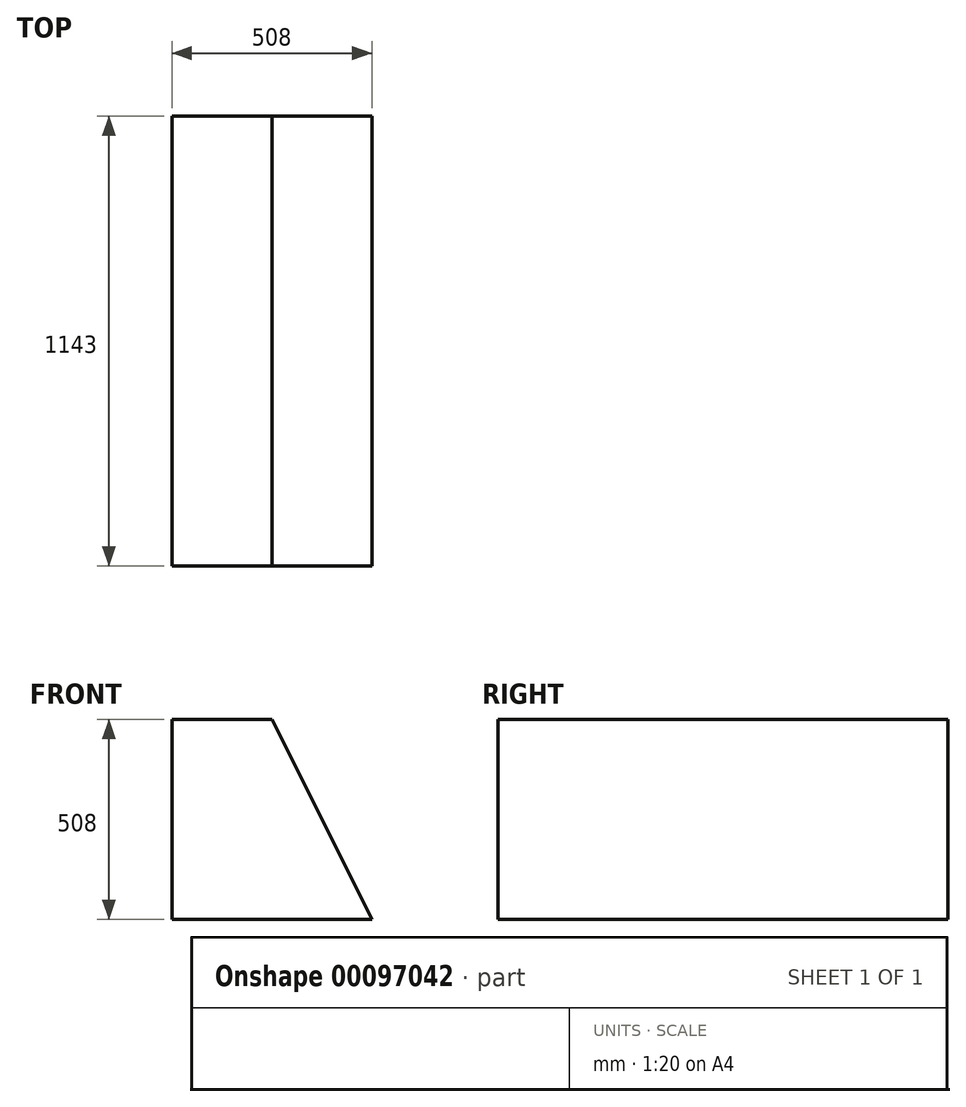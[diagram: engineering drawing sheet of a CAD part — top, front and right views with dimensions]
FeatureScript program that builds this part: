
annotation { "Feature Type Name" : "Feature", "Feature Type Description" : "" }
export const myFeature = defineFeature(function(context is Context, id is Id, definition is map)
    precondition{}
    {
        {
            var Q0;
            Q0=qCreatedBy(makeId("Front.planeOp"),FACE);
            var sketch = newSketch(context, id + "F0", { "sketchPlane" : qUnion([Q0])});
            skLineSegment(sketch, "E0", {"start": v(-36.4, 254.3) * mm, "end": v(-36.4, -253.7) * mm});
            skLineSegment(sketch, "E1", {"start": v(-36.4, -253.7) * mm, "end": v(471.6, -253.7) * mm});
            skLineSegment(sketch, "E2", {"start": v(-36.4, 254.3) * mm, "end": v(217.6, 254.3) * mm});
            skLineSegment(sketch, "E3", {"start": v(217.6, 254.3) * mm, "end": v(471.6, -253.7) * mm});
            skSolve(sketch);
        }
        {
            var Q0;
            Q0 = qSketchRegion(id + "F0", true);
            extrude(context, id + "F1", {"entities" : qUnion([Q0]), "depth" : 1143 * mm});
        }
    });
